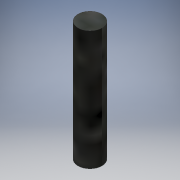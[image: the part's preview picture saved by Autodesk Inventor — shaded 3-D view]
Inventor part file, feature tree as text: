
AUTODESK INVENTOR PART (.ipt)
format: ipt  version: 2017 (Build 210142000, 142)  size: 95,232 bytes
history: native  units: mm
features: other x1, extrude x1, sketch x1
ambient origin geometry x8: Origin, YZ Plane, XZ Plane, XY Plane, X Axis, Y Axis, Z Axis, Center Point
bodies: Body1 (feature_tree)
feature tree (3):
  other  "ソリッド1"
  extrude  "押し出し1"  Depth=2.0mm
  sketch  "スケッチ1"
